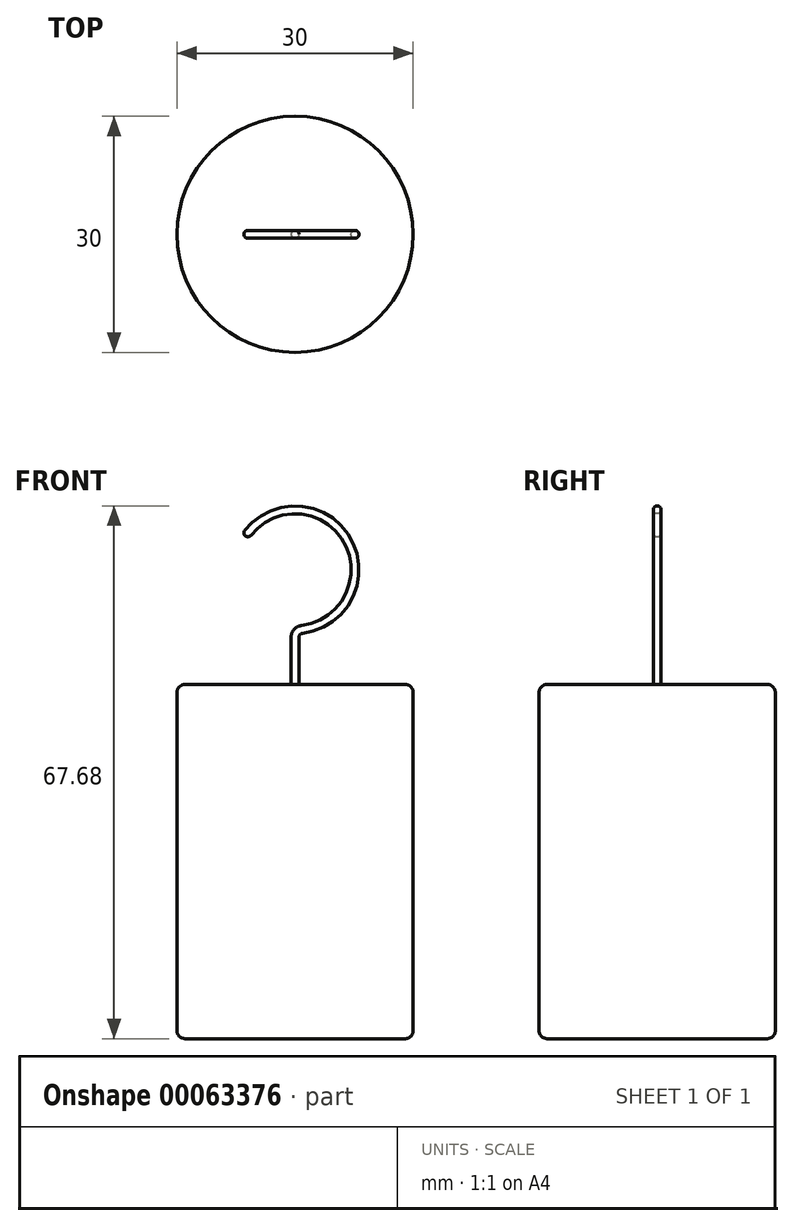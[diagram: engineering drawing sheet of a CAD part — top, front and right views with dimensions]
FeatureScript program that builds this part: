
annotation { "Feature Type Name" : "Feature", "Feature Type Description" : "" }
export const myFeature = defineFeature(function(context is Context, id is Id, definition is map)
    precondition{}
    {
        {
            var Q0;
            Q0=qCreatedBy(makeId("Top.planeOp"),FACE);
            var sketch = newSketch(context, id + "F0", { "sketchPlane" : qUnion([Q0])});
            skCircle(sketch, "E0", {"center": v(0, 0) * mm, "radius": 15 * mm});
            skSolve(sketch);
        }
        {
            var Q0;
            Q0 = qSketchRegion(id + "F0", true);
            extrude(context, id + "F1", {"entities" : qUnion([Q0]), "endBound" : BoundingType.SYMMETRIC, "depth" : 45 * mm});
        }
        {
            var Q0;
            Q0=makeQuery(id+"F1.opExtrude","CAP_FACE",FACE,{"disambiguationData":[OSD([sQuery(id+"F0.wireOp",EDGE,"E0")])],"isStart":false});
            var sketch = newSketch(context, id + "F2", { "sketchPlane" : qUnion([Q0])});
            skCircle(sketch, "E1", {"center": v(0, 0) * mm, "radius": 0.5 * mm});
            skSolve(sketch);
        }
        {
            var Q0;
            Q0=qCreatedBy(makeId("Front.planeOp"),FACE);
            var sketch = newSketch(context, id + "F3", { "sketchPlane" : qUnion([Q0])});
            skLineSegment(sketch, "E2.0", {"start": v(-15, 22.5) * mm, "end": v(15, 22.5) * mm, "construction": true});
            skPoint(sketch, "E3.0", {"position": v(0, 22.5) * mm});
            skLineSegment(sketch, "E4", {"start": v(0, 22.5) * mm, "end": v(0, 28.5) * mm});
            skArc(sketch, "E5", {"start": v(0.88, 29.5) * mm, "mid": v(7.6, 37.5) * mm, "end": v(0, 44.68) * mm});
            skPoint(sketch, "E6.orphan", {"position": v(0, 59.06) * mm});
            skArc(sketch, "E7.filletArc", {"start": v(0.88, 29.5) * mm, "mid": v(0.25, 29.17) * mm, "end": v(0, 28.5) * mm});
            skArc(sketch, "E8", {"start": v(0, 44.68) * mm, "mid": v(-3.56, 43.8) * mm, "end": v(-6.3, 41.35) * mm});
            skLineSegment(sketch, "E9", {"start": v(0, 37.06) * mm, "end": v(-15.04, 47.32) * mm, "construction": true});
            skLineSegment(sketch, "E10", {"start": v(0, 37.06) * mm, "end": v(1, 28.5) * mm, "construction": true});
            skSolve(sketch);
        }
        {
            var Q0;
            Q0 = qSketchRegion(id + "F2", true);
            var Q1;
            Q1 = qConstructionFilter(qBodyType(qCreatedBy(id + "F3" ,EDGE), BodyType.WIRE), ConstructionObject.NO);
            sweep(context, id + "F4", {"operationType" : NewBodyOperationType.ADD, "profiles" : qUnion([Q0]), "path" : qUnion([Q1])});
        }
        {
            var Q0;
            Q0=makeQuery(id+"F1.opExtrude","CAP_EDGE",EDGE,{"disambiguationData":[OSD([sQuery(id+"F0.wireOp",EDGE,"E0")])],"isStart":false});
            var Q1;
            Q1=makeQuery(id+"F1.opExtrude","CAP_EDGE",EDGE,{"disambiguationData":[OSD([sQuery(id+"F0.wireOp",EDGE,"E0")])],"isStart":true});
            fillet(context, id + "F5", {"entities" : qUnion([Q0, Q1]), "radius" : 1 * mm, "tangentPropagation" : true, "allowEdgeOverflow" : false});
        }
        {
            var Q0;
            Q0=makeQuery(id+"F4.opSweep","CAP_FACE",FACE,{"disambiguationData":[OSD([sQuery(id+"F2.wireOp",EDGE,"E1"),sQuery(id+"F3.wireOp",VERTEX,"E8.end")])],"isStart":false});
            fillet(context, id + "F6", {"entities" : qUnion([Q0]), "radius" : 0.5 * mm, "tangentPropagation" : true, "allowEdgeOverflow" : false});
        }
        {
            var Q0;
            Q0=makeQuery(id+"F1.opExtrude","CAP_FACE",FACE,{"disambiguationData":[OSD([sQuery(id+"F0.wireOp",EDGE,"E0")])],"isStart":false});
            cPlane(context, id + "F7", {"entities" : qUnion([Q0]), "cplaneType" : CPlaneType.OFFSET, "offset" : 21.59 * mm, "width" : 152.4 * mm, "height" : 152.4 * mm});
        }
        {
            var Q0;
            Q0=qCreatedBy(id+"F7.planeOp",FACE);
            var sketch = newSketch(context, id + "F8", { "sketchPlane" : qUnion([Q0])});
            skLineSegment(sketch, "E11", {"start": v(7.62, -0.5) * mm, "end": v(-6, -0.5) * mm, "construction": true});
            skLineSegment(sketch, "E12", {"start": v(0.88, 0.5) * mm, "end": v(7.62, 0.5) * mm, "construction": true});
            skArc(sketch, "E13", {"start": v(7.62, 0.5) * mm, "mid": v(7.12, 0) * mm, "end": v(7.62, -0.5) * mm, "construction": true});
            skCircle(sketch, "E14", {"center": v(0, 0) * mm, "radius": 0.5 * mm, "construction": true});
            skSolve(sketch);
        }
    });
